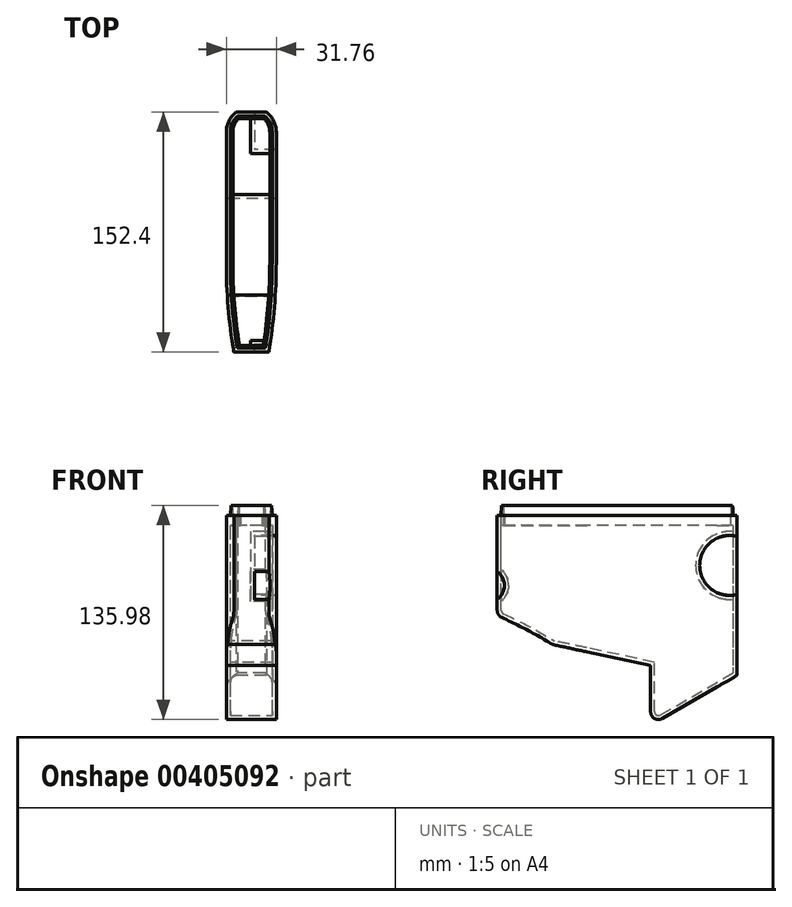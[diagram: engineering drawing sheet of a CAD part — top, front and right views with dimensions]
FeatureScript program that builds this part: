
annotation { "Feature Type Name" : "Feature", "Feature Type Description" : "" }
export const myFeature = defineFeature(function(context is Context, id is Id, definition is map)
    precondition{}
    {
        {
            var Q0;
            Q0=qCreatedBy(makeId("Right.planeOp"),FACE);
            var sketch = newSketch(context, id + "F0", { "sketchPlane" : qUnion([Q0])});
            skLineSegment(sketch, "E0", {"start": v(55, 133.35) * mm, "end": v(-97.4, 133.35) * mm});
            skLineSegment(sketch, "E1", {"start": v(-97.4, 133.35) * mm, "end": v(-97.4, 69.85) * mm});
            skLineSegment(sketch, "E2", {"start": v(55, 133.35) * mm, "end": v(55, 31.75) * mm});
            skArc(sketch, "E3", {"start": v(0, 0) * mm, "mid": v(-45.08, 39.98) * mm, "end": v(-97.4, 69.85) * mm, "construction": true});
            skLineSegment(sketch, "E4", {"start": v(0, 0) * mm, "end": v(55, 31.75) * mm});
            skLineSegment(sketch, "E5", {"start": v(0, 0) * mm, "end": v(0, 38.1) * mm});
            skLineSegment(sketch, "E6", {"start": v(0, 38.1) * mm, "end": v(-62.11, 51.3) * mm});
            skArc(sketch, "E7", {"start": v(-62.11, 51.3) * mm, "mid": v(-79.44, 61.18) * mm, "end": v(-97.4, 69.85) * mm});
            skSolve(sketch);
        }
        {
            var Q0;
            Q0 = qSketchRegion(id + "F0", true);
            extrude(context, id + "F1", {"entities" : qUnion([Q0]), "endBound" : BoundingType.SYMMETRIC, "depth" : 31.75 * mm, "offsetDistance" : 25.4 * mm});
        }
        {
            var Q0;
            Q0=makeQuery(id+"F1.opExtrude","SWEPT_FACE",FACE,{"disambiguationData":[OSD([sQuery(id+"F0.wireOp",EDGE,"E0")])]});
            var sketch = newSketch(context, id + "F2", { "sketchPlane" : qUnion([Q0])});
            skLineSegment(sketch, "E8", {"start": v(0, 0) * mm, "end": v(0, 161.6) * mm, "construction": true});
            skArc(sketch, "E9", {"start": v(11.11, -97.4) * mm, "mid": v(14.68, -68.93) * mm, "end": v(15.88, -40.26) * mm});
            skLineSegment(sketch, "E10", {"start": v(15.88, -40.26) * mm, "end": v(15.88, -97.4) * mm});
            skLineSegment(sketch, "E11", {"start": v(15.88, -97.4) * mm, "end": v(11.11, -97.4) * mm});
            skLineSegment(sketch, "E12.MirrorCS", {"start": v(-15.88, -97.4) * mm, "end": v(-11.11, -97.4) * mm});
            skLineSegment(sketch, "E13.MirrorCS", {"start": v(-15.88, -40.26) * mm, "end": v(-15.88, -97.4) * mm});
            skArc(sketch, "E14.MirrorCS", {"start": v(-11.11, -97.4) * mm, "mid": v(-14.68, -68.93) * mm, "end": v(-15.88, -40.26) * mm});
            skSolve(sketch);
        }
        {
            var Q0;
            Q0 = qSketchRegion(id + "F2", true);
            extrude(context, id + "F3", {"entities" : qUnion([Q0]), "operationType" : NewBodyOperationType.REMOVE, "endBound" : BoundingType.UP_TO_NEXT, "oppositeDirection" : true, "depth" : 25.4 * mm, "offsetDistance" : 25.4 * mm});
        }
        {
            var Q0;
            Q0=qCreatedBy(makeId("Top.planeOp"),FACE);
            var sketch = newSketch(context, id + "F4", { "sketchPlane" : qUnion([Q0])});
            skLineSegment(sketch, "E15.0", {"start": v(15.88, 55) * mm, "end": v(-15.88, 55) * mm, "construction": true});
            skLineSegment(sketch, "E15.1.0", {"start": v(-15.88, 55) * mm, "end": v(-15.88, 55) * mm});
            skLineSegment(sketch, "E15.1.1", {"start": v(-15.88, 55) * mm, "end": v(15.88, 55) * mm, "construction": true});
            skLineSegment(sketch, "E15.1.2", {"start": v(15.88, 55) * mm, "end": v(15.88, 55) * mm});
            skLineSegment(sketch, "E15.1.3", {"start": v(-15.88, 55) * mm, "end": v(15.88, 55) * mm, "construction": true});
            skLineSegment(sketch, "E16", {"start": v(0, 0) * mm, "end": v(0, 34.99) * mm, "construction": true});
            skArc(sketch, "E17", {"start": v(15.88, 42.3) * mm, "mid": v(14.2, 49.4) * mm, "end": v(9.53, 55) * mm});
            skLineSegment(sketch, "E18", {"start": v(15.88, 42.3) * mm, "end": v(15.88, 55) * mm});
            skArc(sketch, "E19.MirrorCS", {"start": v(-15.88, 42.3) * mm, "mid": v(-14.2, 49.4) * mm, "end": v(-9.53, 55) * mm});
            skLineSegment(sketch, "E20.MirrorCS", {"start": v(-15.88, 42.3) * mm, "end": v(-15.88, 55) * mm});
            skLineSegment(sketch, "E21", {"start": v(15.88, 55) * mm, "end": v(9.53, 55) * mm});
            skLineSegment(sketch, "E22", {"start": v(-9.53, 55) * mm, "end": v(-15.88, 55) * mm});
            skSolve(sketch);
        }
        {
            var Q0;
            Q0 = qSketchRegion(id + "F4", true);
            extrude(context, id + "F5", {"entities" : qUnion([Q0]), "operationType" : NewBodyOperationType.REMOVE, "depth" : 139.7 * mm, "offsetDistance" : 25.4 * mm});
        }
        {
            var Q0;
            Q0=qCreatedBy(makeId("Right.planeOp"),FACE);
            cPlane(context, id + "F6", {"entities" : qUnion([Q0]), "cplaneType" : CPlaneType.OFFSET, "offset" : 1.9 * mm, "width" : 152.4 * mm, "height" : 152.4 * mm});
        }
        {
            var Q0;
            Q0=qCreatedBy(id+"F6.planeOp",FACE);
            var sketch = newSketch(context, id + "F7", { "sketchPlane" : qUnion([Q0])});
            skLineSegment(sketch, "E23.0", {"start": v(55, 139.7) * mm, "end": v(55, 31.75) * mm, "construction": true});
            skLineSegment(sketch, "E23.1", {"start": v(-97.4, 69.85) * mm, "end": v(-97.4, 133.35) * mm, "construction": true});
            skArc(sketch, "E24", {"start": v(55, 120.05) * mm, "mid": v(31.18, 101.6) * mm, "end": v(55, 83.15) * mm});
            skArc(sketch, "E25", {"start": v(-97.4, 80.01) * mm, "mid": v(-92.83, 88.9) * mm, "end": v(-97.4, 97.8) * mm});
            skLineSegment(sketch, "E26", {"start": v(-97.4, 97.8) * mm, "end": v(-97.4, 80.01) * mm});
            skLineSegment(sketch, "E27", {"start": v(55, 120.05) * mm, "end": v(55, 83.15) * mm});
            skLineSegment(sketch, "E28", {"start": v(-97.4, 133.35) * mm, "end": v(-97.4, 57.15) * mm, "construction": true});
            skCircle(sketch, "E29", {"center": v(-92.64, 111.13) * mm, "radius": 3.18 * mm, "construction": true});
            skSolve(sketch);
        }
        {
            var Q0;
            Q0 = qSketchRegion(id + "F7", true);
            extrude(context, id + "F8", {"entities" : qUnion([Q0]), "operationType" : NewBodyOperationType.REMOVE, "endBound" : BoundingType.THROUGH_ALL, "depth" : 25.4 * mm, "offsetDistance" : 25.4 * mm});
        }
        {
            var Q0;
            Q0=makeQuery(id+"F1.opExtrude","SWEPT_EDGE",EDGE,{"disambiguationData":[OSD([sQuery(id+"F0.wireOp",EDGE,"E1"),sQuery(id+"F0.wireOp",EDGE,"E7")])]});
            var Q1;
            {var subQ0=sQuery(id+"F0.wireOp",EDGE,"E1");var subQ1=sQuery(id+"F2.wireOp",EDGE,"E14.MirrorCS");Q1=makeQuery(id+"Fqb99eBjwZUgLVf_1.1.F8.boolean.opBoolean","SPLIT",EDGE,{"disambiguationData":[TD([makeQuery(id+"F1.opExtrude","SWEPT_FACE",FACE,{"disambiguationData":[OSD([sQuery(id+"F0.wireOp",EDGE,"E7")])]})])],"derivedFrom":makeQuery(id+"F3.boolean.opBoolean","COPY",EDGE,{"derivedFrom":makeQuery(id+"F3.opExtrude","SWEPT_EDGE",EDGE,{"disambiguationData":[OSD([sQuery(id+"F0.wireOp",EDGE,"E0"),subQ0,sQuery(id+"F2.wireOp",EDGE,"E12.MirrorCS"),subQ1])]})})});}
            var Q2;
            {var subQ0=sQuery(id+"F0.wireOp",EDGE,"E1");var subQ1=sQuery(id+"F2.wireOp",EDGE,"E9");Q2=makeQuery(id+"F8.boolean.opBoolean","SPLIT",EDGE,{"disambiguationData":[TD([makeQuery(id+"F1.opExtrude","SWEPT_FACE",FACE,{"disambiguationData":[OSD([sQuery(id+"F0.wireOp",EDGE,"E7")])]})])],"derivedFrom":makeQuery(id+"F3.boolean.opBoolean","COPY",EDGE,{"derivedFrom":makeQuery(id+"F3.opExtrude","SWEPT_EDGE",EDGE,{"disambiguationData":[OSD([sQuery(id+"F0.wireOp",EDGE,"E0"),subQ0,subQ1,sQuery(id+"F2.wireOp",EDGE,"E11")])]})})});}
            var Q3;
            {var subQ0=sQuery(id+"F0.wireOp",EDGE,"E0");var subQ1=sQuery(id+"F0.wireOp",EDGE,"E1");var subQ2=sQuery(id+"F2.wireOp",EDGE,"E9");Q3=makeQuery(id+"F8.boolean.opBoolean","SPLIT",EDGE,{"disambiguationData":[TD([makeQuery(id+"F1.opExtrude","SWEPT_FACE",FACE,{"disambiguationData":[OSD([subQ0])]})])],"derivedFrom":makeQuery(id+"F3.boolean.opBoolean","COPY",EDGE,{"derivedFrom":makeQuery(id+"F3.opExtrude","SWEPT_EDGE",EDGE,{"disambiguationData":[OSD([subQ0,subQ1,subQ2,sQuery(id+"F2.wireOp",EDGE,"E11")])]})})});}
            var Q4;
            {var subQ0=sQuery(id+"F0.wireOp",EDGE,"E0");var subQ1=sQuery(id+"F2.wireOp",EDGE,"E14.MirrorCS");var subQ2=sQuery(id+"F0.wireOp",EDGE,"E1");Q4=makeQuery(id+"Fqb99eBjwZUgLVf_1.1.F8.boolean.opBoolean","SPLIT",EDGE,{"disambiguationData":[TD([makeQuery(id+"F1.opExtrude","SWEPT_FACE",FACE,{"disambiguationData":[OSD([subQ0])]})])],"derivedFrom":makeQuery(id+"F3.boolean.opBoolean","COPY",EDGE,{"derivedFrom":makeQuery(id+"F3.opExtrude","SWEPT_EDGE",EDGE,{"disambiguationData":[OSD([subQ0,subQ2,sQuery(id+"F2.wireOp",EDGE,"E12.MirrorCS"),subQ1])]})})});}
            var Q5;
            Q5=makeQuery(id+"F1.opExtrude","SWEPT_EDGE",EDGE,{"disambiguationData":[OSD([sQuery(id+"F0.wireOp",EDGE,"E4"),sQuery(id+"F0.wireOp",EDGE,"E5")])]});
            fillet(context, id + "F9", {"entities" : qUnion([Q0, Q1, Q2, Q3, Q4, Q5]), "radius" : 5.08 * mm, "tangentPropagation" : true, "allowEdgeOverflow" : false});
        }
        {
            var Q0;
            Q0=makeQuery(id+"F1.opExtrude","SWEPT_FACE",FACE,{"disambiguationData":[OSD([sQuery(id+"F0.wireOp",EDGE,"E0")])]});
            shell(context, id + "F10", {"entities" : qUnion([Q0]), "thickness" : 2.54 * mm});
        }
        {
            var Q0;
            Q0=makeQuery(id+"F1.opExtrude","SWEPT_FACE",FACE,{"disambiguationData":[OSD([sQuery(id+"F0.wireOp",EDGE,"E0")])]});
            var sketch = newSketch(context, id + "F11", { "sketchPlane" : qUnion([Q0])});
            skLineSegment(sketch, "E30.0", {"start": v(-13.33, 42.3) * mm, "end": v(-13.33, -40.26) * mm});
            skArc(sketch, "E30.1", {"start": v(-9.3, -92.72) * mm, "mid": v(-12.32, -66.56) * mm, "end": v(-13.34, -40.26) * mm});
            skLineSegment(sketch, "E30.2", {"start": v(6.79, -94.87) * mm, "end": v(-6.79, -94.87) * mm});
            skArc(sketch, "E30.3", {"start": v(-9.3, -92.72) * mm, "mid": v(-8.44, -94.26) * mm, "end": v(-6.79, -94.87) * mm});
            skArc(sketch, "E30.4", {"start": v(9.3, -92.72) * mm, "mid": v(12.32, -66.56) * mm, "end": v(13.34, -40.26) * mm});
            skArc(sketch, "E30.5", {"start": v(6.79, -94.87) * mm, "mid": v(8.44, -94.26) * mm, "end": v(9.3, -92.72) * mm});
            skLineSegment(sketch, "E30.6", {"start": v(13.33, 42.3) * mm, "end": v(13.33, -40.26) * mm});
            skArc(sketch, "E30.7", {"start": v(-13.33, 42.3) * mm, "mid": v(-12.1, 47.89) * mm, "end": v(-8.64, 52.45) * mm});
            skLineSegment(sketch, "E30.8", {"start": v(8.64, 52.45) * mm, "end": v(-8.64, 52.45) * mm});
            skArc(sketch, "E30.9", {"start": v(13.33, 42.3) * mm, "mid": v(12.1, 47.89) * mm, "end": v(8.64, 52.45) * mm});
            skArc(sketch, "E31.0", {"start": v(11.75, 42.3) * mm, "mid": v(10.78, 46.96) * mm, "end": v(8.03, 50.87) * mm});
            skLineSegment(sketch, "E31.1", {"start": v(11.75, 42.3) * mm, "end": v(11.75, -40.26) * mm});
            skLineSegment(sketch, "E31.2", {"start": v(8.03, 50.87) * mm, "end": v(-8.03, 50.87) * mm});
            skArc(sketch, "E31.3", {"start": v(7.6, -93.28) * mm, "mid": v(10.7, -66.85) * mm, "end": v(11.75, -40.26) * mm});
            skArc(sketch, "E31.4", {"start": v(-11.75, 42.3) * mm, "mid": v(-10.78, 46.96) * mm, "end": v(-8.03, 50.87) * mm});
            skLineSegment(sketch, "E31.5", {"start": v(-11.75, 42.3) * mm, "end": v(-11.75, -40.26) * mm});
            skArc(sketch, "E31.6", {"start": v(-7.6, -93.28) * mm, "mid": v(-10.7, -66.85) * mm, "end": v(-11.75, -40.26) * mm});
            skLineSegment(sketch, "E31.7", {"start": v(7.6, -93.28) * mm, "end": v(-7.6, -93.28) * mm});
            skSolve(sketch);
        }
        {
            var Q0;
            Q0 = qSketchRegion(id + "F11", true);
            extrude(context, id + "F12", {"entities" : qUnion([Q0]), "operationType" : NewBodyOperationType.ADD, "depth" : 6.35 * mm, "offsetDistance" : 25.4 * mm, "hasDraft" : true, "draftAngle" : 3 * degree, "draftPullDirection" : true, "hasSecondDirection" : true, "secondDirectionOppositeDirection" : true, "secondDirectionDepth" : 6.35 * mm});
        }
    });
